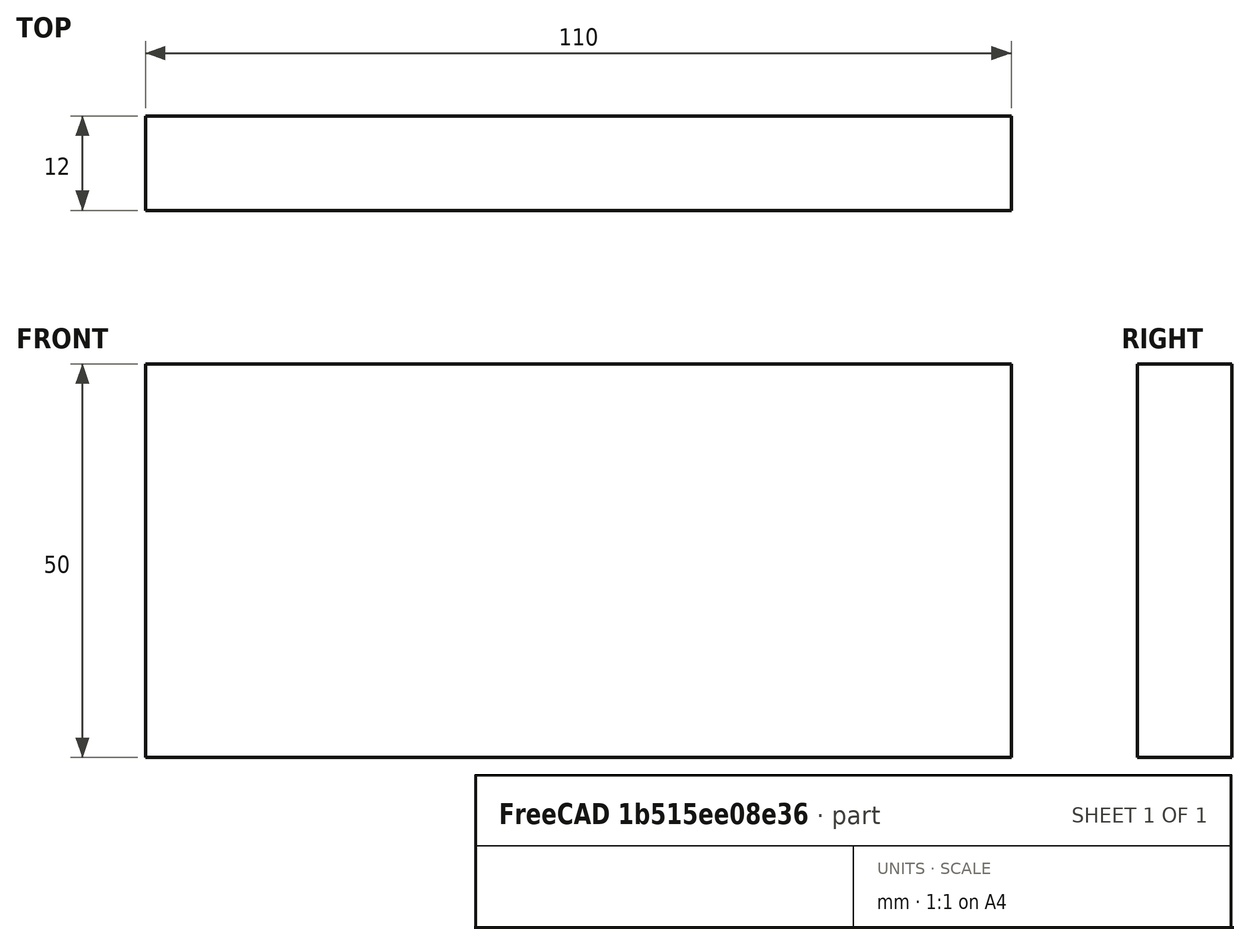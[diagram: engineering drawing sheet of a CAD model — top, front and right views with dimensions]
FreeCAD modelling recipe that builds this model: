
FCSTD DOCUMENT  (FreeCAD 0.15R4671 (Git))
Label: Flat Bar 110x12 EN10058 S235JR
License: All rights reserved
LicenseURL: http://en.wikipedia.org/wiki/All_rights_reserved
objects: Sketcher::SketchObject×1, Part::Extrusion×1
note: 2 computed .brp shape members not serialized (recipe doc carries the construction recipe); baked Part::Feature solids carry a one-line shape summary decoded from their .brp

FEATURE [Sketcher::SketchObject] Sketch
  sketch-geometry (4):
    g0: LineSegment StartX=-55 StartY=-6 StartZ=0 EndX=55 EndY=-6 EndZ=0
    g1: LineSegment StartX=55 StartY=-6 StartZ=0 EndX=55 EndY=6 EndZ=0
    g2: LineSegment StartX=55 StartY=6 StartZ=0 EndX=-55 EndY=6 EndZ=0
    g3: LineSegment StartX=-55 StartY=6 StartZ=0 EndX=-55 EndY=-6 EndZ=0
  constraints (12):
    c: Coincident(g0,g1)
    c: Coincident(g1,g2)
    c: Coincident(g2,g3)
    c: Coincident(g3,g0)
    c: Horizontal(g0)
    c: Horizontal(g2)
    c: Vertical(g1)
    c: Vertical(g3)
    c: Symmetric(g1,g2,g-2)
    c: Symmetric(g0,g1,g-1)
    c: DistanceY(g1) = 12
    c: DistanceX(g0) = 110
FEATURE [Part::Extrusion] Extrude  label="Flat Bar 110x12 EN10058 S235JR"
  Base = -> Sketch
  Dir = (0,0,50)
  Solid = true
